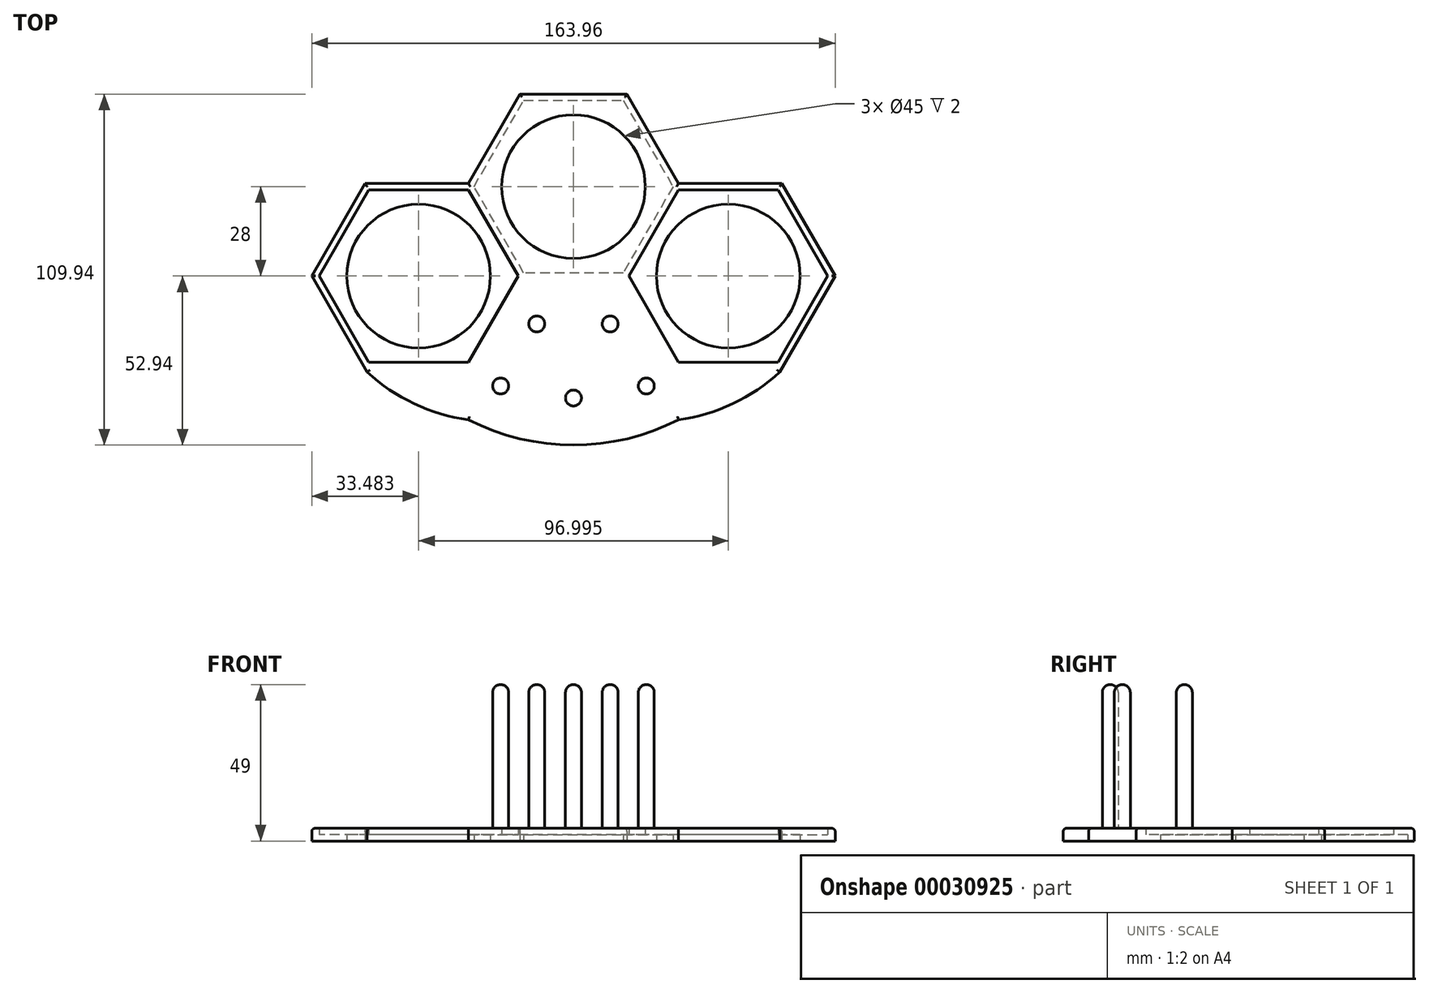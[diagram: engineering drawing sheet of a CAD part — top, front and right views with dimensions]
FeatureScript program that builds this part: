
annotation { "Feature Type Name" : "Feature", "Feature Type Description" : "" }
export const myFeature = defineFeature(function(context is Context, id is Id, definition is map)
    precondition{}
    {
        {
            var Q0;
            Q0=qCreatedBy(makeId("Top.planeOp"),FACE);
            var sketch = newSketch(context, id + "F0", { "sketchPlane" : qUnion([Q0])});
            skLineSegment(sketch, "E0.5", {"start": v(-15.59, 83) * mm, "end": v(15.59, 83) * mm});
            skLineSegment(sketch, "E1.5", {"start": v(-64.09, 55) * mm, "end": v(-32.9, 55) * mm});
            skCircle(sketch, "E2", {"center": v(0, 56) * mm, "radius": 22.5 * mm});
            skLineSegment(sketch, "E1.3", {"start": v(-64.09, 1) * mm, "end": v(-79.67, 28) * mm});
            skPoint(sketch, "E1.0.midPoint", {"position": v(-25.11, 41.5) * mm});
            skPoint(sketch, "E3.0.midPoint", {"position": v(23.38, 13.5) * mm});
            skPoint(sketch, "E0.0.midPoint", {"position": v(23.38, 69.5) * mm});
            skCircle(sketch, "E4", {"center": v(-48.5, 28) * mm, "radius": 22.5 * mm});
            skLineSegment(sketch, "E1.0", {"start": v(-32.9, 55) * mm, "end": v(-17.32, 28) * mm});
            skLineSegment(sketch, "E0.3", {"start": v(-15.59, 29) * mm, "end": v(-31.18, 56) * mm});
            skPoint(sketch, "E5.0.midPoint", {"position": v(71.88, 41.5) * mm});
            skCircle(sketch, "E1.cCircle", {"center": v(-48.5, 28) * mm, "radius": 27 * mm, "construction": true});
            skLineSegment(sketch, "E0.0", {"start": v(15.59, 83) * mm, "end": v(31.18, 56) * mm});
            skLineSegment(sketch, "E5.3", {"start": v(32.9, 1) * mm, "end": v(17.32, 28) * mm});
            skLineSegment(sketch, "E5.0", {"start": v(64.09, 55) * mm, "end": v(79.67, 28) * mm});
            skCircle(sketch, "E5.cCircle", {"center": v(48.5, 28) * mm, "radius": 27 * mm, "construction": true});
            skLineSegment(sketch, "E5.4", {"start": v(17.32, 28) * mm, "end": v(32.9, 55) * mm});
            skLineSegment(sketch, "E5.1", {"start": v(79.67, 28) * mm, "end": v(64.09, 1) * mm});
            skLineSegment(sketch, "E5.2", {"start": v(64.09, 1) * mm, "end": v(32.9, 1) * mm});
            skLineSegment(sketch, "E5.5", {"start": v(32.9, 55) * mm, "end": v(64.09, 55) * mm});
            skCircle(sketch, "E6", {"center": v(48.5, 28) * mm, "radius": 22.5 * mm});
            skCircle(sketch, "E0.cCircle", {"center": v(0, 56) * mm, "radius": 27 * mm, "construction": true});
            skLineSegment(sketch, "E1.4", {"start": v(-79.67, 28) * mm, "end": v(-64.09, 55) * mm});
            skLineSegment(sketch, "E0.1", {"start": v(31.18, 56) * mm, "end": v(15.59, 29) * mm});
            skPoint(sketch, "E7.0.midPoint", {"position": v(71.88, -14.5) * mm});
            skLineSegment(sketch, "E1.1", {"start": v(-17.32, 28) * mm, "end": v(-32.9, 1) * mm});
            skLineSegment(sketch, "E0.2", {"start": v(15.59, 29) * mm, "end": v(-15.59, 29) * mm});
            skLineSegment(sketch, "E8", {"start": v(-15.59, 27) * mm, "end": v(-17.32, 28) * mm, "construction": true});
            skLineSegment(sketch, "E9", {"start": v(-64.09, 1) * mm, "end": v(-32.9, 1) * mm});
            skLineSegment(sketch, "E10", {"start": v(-81.98, 28) * mm, "end": v(-98.02, 28) * mm, "construction": true});
            skLineSegment(sketch, "E11", {"start": v(-31.18, 56) * mm, "end": v(-15.59, 83) * mm});
            skLineSegment(sketch, "E12", {"start": v(81.98, 28) * mm, "end": v(98.89, 28) * mm, "construction": true});
            skLineSegment(sketch, "E13", {"start": v(-17.32, 28) * mm, "end": v(17.32, 28) * mm, "construction": true});
            skLineSegment(sketch, "E14", {"start": v(0, 29) * mm, "end": v(0, 28) * mm, "construction": true});
            skCircle(sketch, "E15", {"center": v(-11.5, 13) * mm, "radius": 2.5 * mm});
            skCircle(sketch, "E16", {"center": v(11.5, 13) * mm, "radius": 2.5 * mm});
            skCircle(sketch, "E17", {"center": v(-22.81, -6.43) * mm, "radius": 2.5 * mm});
            skCircle(sketch, "E18", {"center": v(0, -10.2) * mm, "radius": 2.5 * mm});
            skCircle(sketch, "E19", {"center": v(22.81, -6.43) * mm, "radius": 2.5 * mm});
            skLineSegment(sketch, "E20", {"start": v(0, 0) * mm, "end": v(0, 23.32) * mm, "construction": true});
            skLineSegment(sketch, "E21", {"start": v(-11.5, 13) * mm, "end": v(0, -10.2) * mm, "construction": true});
            skLineSegment(sketch, "E22", {"start": v(11.5, 13) * mm, "end": v(0, -10.2) * mm, "construction": true});
            skLineSegment(sketch, "E23", {"start": v(11.5, 13) * mm, "end": v(22.81, -6.43) * mm, "construction": true});
            skLineSegment(sketch, "E24", {"start": v(-11.5, 13) * mm, "end": v(-22.81, -6.43) * mm, "construction": true});
            skLineSegment(sketch, "E25", {"start": v(-22.81, -6.43) * mm, "end": v(0, -10.2) * mm, "construction": true});
            skLineSegment(sketch, "E26", {"start": v(0, -10.2) * mm, "end": v(22.81, -6.43) * mm, "construction": true});
            skCircle(sketch, "E27", {"center": v(-22.81, -6.43) * mm, "radius": 10.5 * mm, "construction": true});
            skCircle(sketch, "E28", {"center": v(22.81, -6.43) * mm, "radius": 10.5 * mm, "construction": true});
            skCircle(sketch, "E29", {"center": v(0, -10.2) * mm, "radius": 10.5 * mm, "construction": true});
            skArc(sketch, "E30", {"start": v(-32.9, -17) * mm, "mid": v(0, -24.94) * mm, "end": v(32.9, -17) * mm});
            skArc(sketch, "E31", {"start": v(-81.98, 28) * mm, "mid": v(-64.5, -2.2) * mm, "end": v(-32.9, -17) * mm});
            skArc(sketch, "E32.MirrorCS", {"start": v(81.98, 28) * mm, "mid": v(64.5, -2.2) * mm, "end": v(32.9, -17) * mm});
            skArc(sketch, "E33", {"start": v(-68.4, 61.79) * mm, "mid": v(-37.17, 63.25) * mm, "end": v(-17.83, 87.8) * mm});
            skLineSegment(sketch, "E34", {"start": v(-32.9, 57) * mm, "end": v(-65.24, 57) * mm});
            skLineSegment(sketch, "E35", {"start": v(-65.24, 57) * mm, "end": v(-81.98, 28) * mm});
            skLineSegment(sketch, "E36", {"start": v(-32.9, 57) * mm, "end": v(-16.74, 85) * mm});
            skLineSegment(sketch, "E37", {"start": v(-16.74, 85) * mm, "end": v(16.74, 85) * mm});
            skLineSegment(sketch, "E38", {"start": v(16.74, 85) * mm, "end": v(32.9, 57) * mm});
            skLineSegment(sketch, "E39", {"start": v(32.9, 57) * mm, "end": v(65.24, 57) * mm});
            skLineSegment(sketch, "E40", {"start": v(65.24, 57) * mm, "end": v(81.98, 28) * mm});
            skEllipticalArc(sketch, "E41", {});
            skEllipticalArc(sketch, "E42", {});
            skLineSegment(sketch, "E43", {"start": v(-81.98, 28) * mm, "end": v(-64.5, -2.28) * mm});
            skPoint(sketch, "E43.endSnap0", {"position": v(-64.5, -2.2) * mm});
            skLineSegment(sketch, "E44.MirrorCS", {"start": v(81.98, 28) * mm, "end": v(64.5, -2.28) * mm});
            const initialGuessF0  = {"E41": [0, 0.028, -1, 0, 0.08198373822595166, 0.06126651134421153, 0, 3.141592653589793], "E42": [0, 0.028, -1, 0, 0.08198373822595166, 0.06126651134421153, 3.141592653589793, 0]};
            skSetInitialGuess(sketch, initialGuessF0);
            skSolve(sketch);
        }
        {
            var Q0;
            Q0=makeQuery(id+"F0.imprint","IMPRINT",FACE,{"disambiguationData":[TD([[makeQuery(id+"F0.imprint","IMPRINT",EDGE,{"derivedFrom":sQuery(id+"F0.wireOp",EDGE,"E0.5")}),1.0]])]});
            var Q1;
            Q1=makeQuery(id+"F0.imprint","IMPRINT",FACE,{"disambiguationData":[TD([[makeQuery(id+"F0.imprint","IMPRINT",EDGE,{"derivedFrom":sQuery(id+"F0.wireOp",EDGE,"E1.5")}),-1.0]])]});
            var Q2;
            Q2=makeQuery(id+"F0.imprint","IMPRINT",FACE,{"disambiguationData":[TD([[makeQuery(id+"F0.imprint","IMPRINT",EDGE,{"derivedFrom":sQuery(id+"F0.wireOp",EDGE,"E5.3")}),-1.0]])]});
            extrude(context, id + "F1", {"entities" : qUnion([Q0, Q1, Q2]), "depth" : 2 * mm});
        }
        {
            var Q0;
            Q0=makeQuery(id+"F0.imprint","IMPRINT",FACE,{"disambiguationData":[TD([[makeQuery(id+"F0.imprint","IMPRINT",EDGE,{"derivedFrom":sQuery(id+"F0.wireOp",EDGE,"E0.5")}),1.0]])]});
            extrude(context, id + "F2", {"entities" : qUnion([Q0]), "operationType" : NewBodyOperationType.ADD, "depth" : 4 * mm});
        }
        {
            var Q0;
            Q0=makeQuery(id+"F0.imprint","IMPRINT",FACE,{"disambiguationData":[TD([[makeQuery(id+"F0.imprint","IMPRINT",EDGE,{"derivedFrom":sQuery(id+"F0.wireOp",EDGE,"E15")}),1.0]])]});
            var Q1;
            Q1=makeQuery(id+"F0.imprint","IMPRINT",FACE,{"disambiguationData":[TD([[makeQuery(id+"F0.imprint","IMPRINT",EDGE,{"derivedFrom":sQuery(id+"F0.wireOp",EDGE,"E16")}),1.0]])]});
            var Q2;
            Q2=makeQuery(id+"F0.imprint","IMPRINT",FACE,{"disambiguationData":[TD([[makeQuery(id+"F0.imprint","IMPRINT",EDGE,{"derivedFrom":sQuery(id+"F0.wireOp",EDGE,"E17")}),1.0]])]});
            var Q3;
            Q3=makeQuery(id+"F0.imprint","IMPRINT",FACE,{"disambiguationData":[TD([[makeQuery(id+"F0.imprint","IMPRINT",EDGE,{"derivedFrom":sQuery(id+"F0.wireOp",EDGE,"E18")}),1.0]])]});
            var Q4;
            Q4=makeQuery(id+"F0.imprint","IMPRINT",FACE,{"disambiguationData":[TD([[makeQuery(id+"F0.imprint","IMPRINT",EDGE,{"derivedFrom":sQuery(id+"F0.wireOp",EDGE,"E19")}),1.0]])]});
            extrude(context, id + "F3", {"entities" : qUnion([Q0, Q1, Q2, Q3, Q4]), "operationType" : NewBodyOperationType.ADD, "depth" : 49 * mm});
        }
        {
            var Q0;
            Q0=makeQuery(id+"F0.imprint","IMPRINT",FACE,{"disambiguationData":[TD([[makeQuery(id+"F0.imprint","IMPRINT",EDGE,{"derivedFrom":sQuery(id+"F0.wireOp",EDGE,"E0.5")}),-1.0]])]});
            extrude(context, id + "F4", {"entities" : qUnion([Q0]), "operationType" : NewBodyOperationType.ADD, "depth" : 4 * mm, "hasSecondDirection" : true, "secondDirectionOppositeDirection" : false, "secondDirectionDepth" : 2 * mm});
        }
        {
            var Q0;
            Q0=makeQuery(id+"F3.opExtrude","CAP_FACE",FACE,{"disambiguationData":[OSD([sQuery(id+"F0.wireOp",EDGE,"E17")])],"isStart":false});
            var Q1;
            Q1=makeQuery(id+"F3.opExtrude","CAP_FACE",FACE,{"disambiguationData":[OSD([sQuery(id+"F0.wireOp",EDGE,"E15")])],"isStart":false});
            var Q2;
            Q2=makeQuery(id+"F3.opExtrude","CAP_FACE",FACE,{"disambiguationData":[OSD([sQuery(id+"F0.wireOp",EDGE,"E16")])],"isStart":false});
            var Q3;
            Q3=makeQuery(id+"F3.opExtrude","CAP_FACE",FACE,{"disambiguationData":[OSD([sQuery(id+"F0.wireOp",EDGE,"E19")])],"isStart":false});
            var Q4;
            Q4=makeQuery(id+"F3.opExtrude","CAP_FACE",FACE,{"disambiguationData":[OSD([sQuery(id+"F0.wireOp",EDGE,"E18")])],"isStart":false});
            fillet(context, id + "F5", {"entities" : qUnion([Q0, Q1, Q2, Q3, Q4]), "radius" : 2.5 * mm, "tangentPropagation" : true, "allowEdgeOverflow" : false});
        }
        {
            var Q0;
            Q0=makeQuery(id+"F2.opExtrude","CAP_EDGE",EDGE,{"disambiguationData":[OSD([sQuery(id+"F0.wireOp",EDGE,"E43")])],"isStart":false});
            var Q1;
            Q1=makeQuery(id+"F2.opExtrude","CAP_EDGE",EDGE,{"disambiguationData":[OSD([sQuery(id+"F0.wireOp",EDGE,"E31")])],"isStart":false});
            var Q2;
            Q2=makeQuery(id+"F2.opExtrude","CAP_EDGE",EDGE,{"disambiguationData":[OSD([sQuery(id+"F0.wireOp",EDGE,"E30")])],"isStart":false});
            var Q3;
            Q3=makeQuery(id+"F2.opExtrude","CAP_EDGE",EDGE,{"disambiguationData":[OSD([sQuery(id+"F0.wireOp",EDGE,"E32.MirrorCS")])],"isStart":false});
            var Q4;
            Q4=makeQuery(id+"F2.opExtrude","CAP_EDGE",EDGE,{"disambiguationData":[OSD([sQuery(id+"F0.wireOp",EDGE,"E44.MirrorCS")])],"isStart":false});
            var Q5;
            Q5=makeQuery(id+"F2.opExtrude","CAP_EDGE",EDGE,{"disambiguationData":[OSD([sQuery(id+"F0.wireOp",EDGE,"E40")])],"isStart":false});
            var Q6;
            Q6=makeQuery(id+"F2.opExtrude","CAP_EDGE",EDGE,{"disambiguationData":[OSD([sQuery(id+"F0.wireOp",EDGE,"E39")])],"isStart":false});
            var Q7;
            Q7=makeQuery(id+"F2.opExtrude","CAP_EDGE",EDGE,{"disambiguationData":[OSD([sQuery(id+"F0.wireOp",EDGE,"E38")])],"isStart":false});
            var Q8;
            Q8=makeQuery(id+"F2.opExtrude","CAP_EDGE",EDGE,{"disambiguationData":[OSD([sQuery(id+"F0.wireOp",EDGE,"E37")])],"isStart":false});
            var Q9;
            Q9=makeQuery(id+"F2.opExtrude","CAP_EDGE",EDGE,{"disambiguationData":[OSD([sQuery(id+"F0.wireOp",EDGE,"E36")])],"isStart":false});
            var Q10;
            Q10=makeQuery(id+"F2.opExtrude","CAP_EDGE",EDGE,{"disambiguationData":[OSD([sQuery(id+"F0.wireOp",EDGE,"E34")])],"isStart":false});
            var Q11;
            Q11=makeQuery(id+"F2.opExtrude","CAP_EDGE",EDGE,{"disambiguationData":[OSD([sQuery(id+"F0.wireOp",EDGE,"E35")])],"isStart":false});
            fillet(context, id + "F6", {"entities" : qUnion([Q0, Q1, Q2, Q3, Q4, Q5, Q6, Q7, Q8, Q9, Q10, Q11]), "radius" : 1 * mm, "tangentPropagation" : true, "allowEdgeOverflow" : false});
        }
    });
